# Revit family: RN 85144 Optiflex-Profix-Té
name_source: partatom
category: Rohrformteile
units: mm (PartAtom-declared; Revit-internal decimal feet)

## family parameters
Arbeitsebenenbasiert = Nein
Beim Laden mit Abzugskörper schneiden = Nein
Bemaßung runder Anschluss = Durchmesser verwenden
Gemeinsam genutzt = Nein
Immer vertikal = Ja
Teiletyp = T-Stück

## types (3) — shared parameters
1.010.00.2 Blattnummer der Richtlinie = 29
1.010.00.3 Ausgabedatum (Monat) der Richtlinie = 201308
1.010.00.4 Herstellername = R. Nussbaum AG
1.010.00.5 Revisionsdatum der Datei = 20190521
1.010.00.6 Webadresse des Herstellers = http://www.nussbaum.ch
1.100.00.4 Produktbezeichnung = Versorgung
1.110.00.2 Index = 5
1.110.00.4 Produktbezeichnung = Optiflex
1.800.00.3 TGA-Nummer = 01900500000000000000000000000000000000000000000057000000000000000001
1.800.00.4 Kommentarfeld = 85144.21, Optiflex-Profix-T-Stück, mit Aussengewinde, DN=20x15x15, L=86, R=¾
1.810.00.3 Hersteller-Bestellnummer = 85144.21
1.810.00.4 DATANORM-Nummer = 85144.21
1.810.00.5 StLB-Nummer = 331.661
1.810.00.6 GTIN-Nummer = 7612945701923
1.960/3L.00.8 Link (URL) = https://www.nussbaum.ch
29.700.00.4 Produktname = Optiflex-Profix-T-Stück, mit Aussengewinde
29.700.00.5 Produktkennung = 2
29.700.00.6 Querschnittsform = 1
29.700.00.7 Nennweitensystem = DN
29.700.00.8 Nenndrucksystem = PN
29.710.02.10 Formstück-Gewicht [kg] = 0.185
29.710.02.3 Benennung = Optiflex-Profix-T-Stück, mit Aussengewinde, DN=20x15x15, L=86, R=¾
29.710.02.4 Nenndruck = 10
29.710.02.5 max. zul. Überdruck [hPa] = 1000
29.710.02.7 max. zul. Dauer-Betriebsdruck [hPa] = 1000
29.710.02.9 max. zul. Dauer-Betriebstemperatur [°C] = 70
CONNECTOR0_DIAMETER_dY_0r = 20 mm
CONNECTOR0_dY_00 = 19 mm
CONNECTOR0_dY_01 = 34 mm
CONNECTOR0_ref_dY = 34 mm
CONNECTOR1_DIAMETER_dY_0r = 12 mm  [stored 0.0393701 ft]
CONNECTOR1_dY_00 = 52 mm
CONNECTOR1_dY_01 = 18 mm
CONNECTOR1_ref_dY = 18 mm
CONNECTOR2_DIAMETER_dX_0r = 12 mm  [stored 0.0393701 ft]
CONNECTOR2_dX_00 = 52 mm
CONNECTOR2_dX_01 = 18 mm
CONNECTOR2_ref_dX = 18 mm
Connector Visibility = Nein
EnclosingSpace Visibility = Nein
Hersteller = R. Nussbaum AG
Modell = 85144.21
R. Nussbaum AG 85144.21 de Visibility = Ja
R. Nussbaum AG 85144.22 de Visibility = Nein
R. Nussbaum AG 85144.23 de Visibility = Nein
Typenkommentare = Optiflex-Profix-Té  DN=20x15x15
URL = https://www.nussbaum.ch

## type names (no varying parameters)
- DN=20x15x15
- DN=20x15x2
- DN=20x15x1

note: [stored X ft] marks values corroborated as IEEE doubles in the binary element streams (Revit-internal decimal feet)

## geometry (parser evidence)
native form markers: Sweep x1
no freeform markers — native parametric forms only
